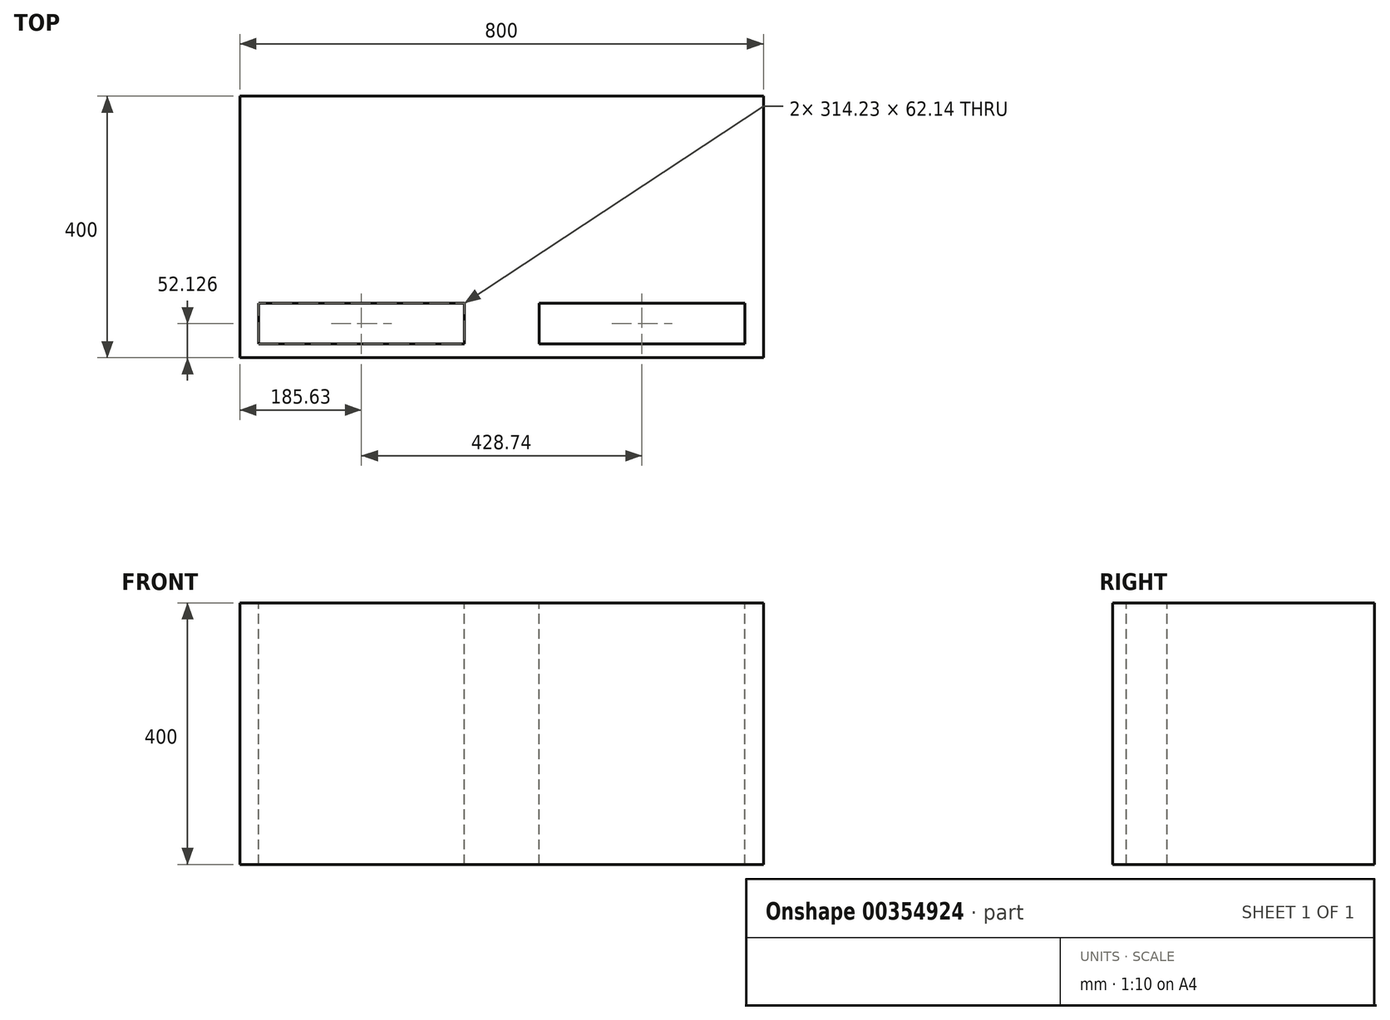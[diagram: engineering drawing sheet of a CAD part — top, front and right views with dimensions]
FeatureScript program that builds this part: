
annotation { "Feature Type Name" : "Feature", "Feature Type Description" : "" }
export const myFeature = defineFeature(function(context is Context, id is Id, definition is map)
    precondition{}
    {
        {
            var Q0;
            Q0=qCreatedBy(makeId("Top.planeOp"),FACE);
            var sketch = newSketch(context, id + "F0", { "sketchPlane" : qUnion([Q0])});
            skLineSegment(sketch, "E0.bottom", {"start": v(0, 0) * mm, "end": v(800, 0) * mm});
            skLineSegment(sketch, "E0.top", {"start": v(0, -400) * mm, "end": v(800, -400) * mm});
            skLineSegment(sketch, "E0.left", {"start": v(0, 0) * mm, "end": v(0, -400) * mm});
            skLineSegment(sketch, "E0.right", {"start": v(800, 0) * mm, "end": v(800, -400) * mm});
            skSolve(sketch);
        }
        {
            var Q0;
            Q0 = qSketchRegion(id + "F0", true);
            extrude(context, id + "F1", {"entities" : qUnion([Q0]), "depth" : 400 * mm});
        }
        {
            var Q0;
            Q0=makeQuery(id+"F1.opExtrude","CAP_FACE",FACE,{"disambiguationData":[OSD([sQuery(id+"F0.wireOp",EDGE,"E0.bottom"),sQuery(id+"F0.wireOp",EDGE,"E0.top"),sQuery(id+"F0.wireOp",EDGE,"E0.left"),sQuery(id+"F0.wireOp",EDGE,"E0.right")])],"isStart":false});
            var sketch = newSketch(context, id + "F2", { "sketchPlane" : qUnion([Q0])});
            skLineSegment(sketch, "E1.bottom", {"start": v(457.26, -316.8) * mm, "end": v(771.48, -316.8) * mm});
            skLineSegment(sketch, "E1.top", {"start": v(457.26, -378.94) * mm, "end": v(771.48, -378.94) * mm});
            skLineSegment(sketch, "E1.left", {"start": v(457.26, -316.8) * mm, "end": v(457.26, -378.94) * mm});
            skLineSegment(sketch, "E1.right", {"start": v(771.48, -316.8) * mm, "end": v(771.48, -378.94) * mm});
            skLineSegment(sketch, "E2.MirrorCS", {"start": v(342.74, -316.8) * mm, "end": v(28.52, -316.8) * mm});
            skLineSegment(sketch, "E3.MirrorCS", {"start": v(342.74, -316.8) * mm, "end": v(342.74, -378.94) * mm});
            skLineSegment(sketch, "E4.MirrorCS", {"start": v(342.74, -378.94) * mm, "end": v(28.52, -378.94) * mm});
            skLineSegment(sketch, "E5.MirrorCS", {"start": v(28.52, -316.8) * mm, "end": v(28.52, -378.94) * mm});
            skPoint(sketch, "E6.orphan", {"position": v(0, -200) * mm});
            skPoint(sketch, "E7.end.orphan", {"position": v(800, -200) * mm});
            skPoint(sketch, "E7.start.orphan", {"position": v(400, -200) * mm});
            skPoint(sketch, "E8.end.orphan", {"position": v(400, -400) * mm});
            skPoint(sketch, "E9.end.orphan", {"position": v(800, -300) * mm});
            skPoint(sketch, "E9.start.orphan", {"position": v(400, -300) * mm});
            skSolve(sketch);
        }
        {
            var Q0;
            Q0 = qSketchRegion(id + "F2", true);
            extrude(context, id + "F3", {"entities" : qUnion([Q0]), "operationType" : NewBodyOperationType.REMOVE, "endBound" : BoundingType.THROUGH_ALL, "oppositeDirection" : true, "depth" : 25 * mm});
        }
    });
